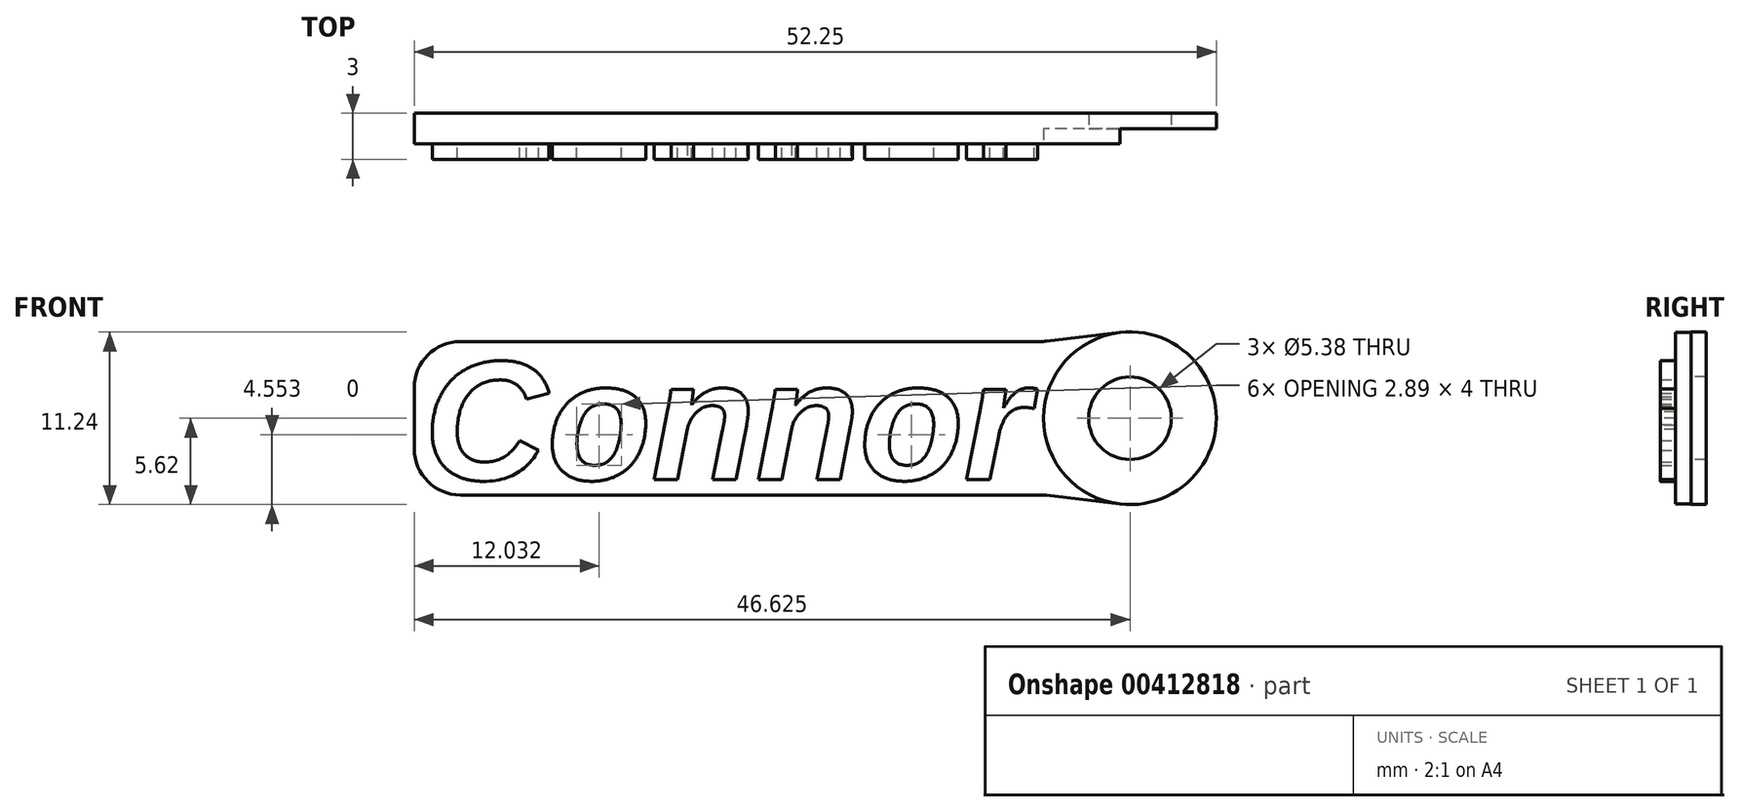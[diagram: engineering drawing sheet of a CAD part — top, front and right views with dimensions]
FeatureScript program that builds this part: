
annotation { "Feature Type Name" : "Feature", "Feature Type Description" : "" }
export const myFeature = defineFeature(function(context is Context, id is Id, definition is map)
    precondition{}
    {
        {
            var Q0;
            Q0=qCreatedBy(makeId("Front.planeOp"),FACE);
            var sketch = newSketch(context, id + "F0", { "sketchPlane" : qUnion([Q0])});
            skText(sketch, "E0", { "text": "Connor", "fontName": "Arimo-BoldItalic.ttf"});
            const initialGuessF0  = {"E0": [-0.02038, -0.008, 1, 0, 0.008]};
            skSetInitialGuess(sketch, initialGuessF0);
            skSolve(sketch);
        }
        {
            var Q0;
            Q0=qSketchRegion(id+"F0",true);
            extrude(context, id + "F1", {"entities" : qUnion([Q0]), "depth" : 1 * mm});
        }
        {
            var Q0;
            Q0=qCreatedBy(makeId("Front.planeOp"),FACE);
            var sketch = newSketch(context, id + "F2", { "sketchPlane" : qUnion([Q0])});
            skLineSegment(sketch, "E1", {"start": v(20, -9) * mm, "end": v(-21, -9) * mm});
            skLineSegment(sketch, "E2", {"start": v(-21, 1) * mm, "end": v(20, 1) * mm});
            skLineSegment(sketch, "E3", {"start": v(20, -9) * mm, "end": v(20, 1) * mm, "construction": true});
            skLineSegment(sketch, "E4", {"start": v(-21, -9) * mm, "end": v(-21, 1) * mm});
            skCircle(sketch, "E5", {"center": v(25.63, -4) * mm, "radius": 5.62 * mm});
            skLineSegment(sketch, "E6", {"start": v(20, -4) * mm, "end": v(67.35, -4) * mm, "construction": true});
            skPoint(sketch, "E6.endSnap0", {"position": v(20, -4) * mm});
            skLineSegment(sketch, "E7", {"start": v(20, 1) * mm, "end": v(24.97, 1.59) * mm});
            skLineSegment(sketch, "E8", {"start": v(24.97, -9.59) * mm, "end": v(20, -9) * mm});
            skCircle(sketch, "E9", {"center": v(25.63, -4) * mm, "radius": 2.69 * mm});
            skLineSegment(sketch, "E10", {"start": v(-20.38, 0) * mm, "end": v(-20.38, 1) * mm, "construction": true});
            skLineSegment(sketch, "E11", {"start": v(-20.38, -8) * mm, "end": v(-20.38, -9) * mm, "construction": true});
            skSolve(sketch);
        }
        {
            var Q0;
            Q0=qSketchRegion(id+"F2",true);
            extrude(context, id + "F3", {"entities" : qUnion([Q0]), "oppositeDirection" : true, "depth" : 2 * mm});
        }
        {
            var Q0;
            Q0=makeQuery(id+"F3.opExtrude","SWEPT_EDGE",EDGE,{"disambiguationData":[OSD([sQuery(id+"F2.wireOp",EDGE,"E2"),sQuery(id+"F2.wireOp",EDGE,"E4")])]});
            var Q1;
            Q1=makeQuery(id+"F3.opExtrude","SWEPT_EDGE",EDGE,{"disambiguationData":[OSD([sQuery(id+"F2.wireOp",EDGE,"E1"),sQuery(id+"F2.wireOp",EDGE,"E4")])]});
            var Q2;
            Q2=makeQuery(id+"F3.opExtrude","SWEPT_EDGE",EDGE,{"disambiguationData":[OSD([sQuery(id+"F2.wireOp",EDGE,"E1"),sQuery(id+"F2.wireOp",EDGE,"E8")])]});
            var Q3;
            Q3=makeQuery(id+"F3.opExtrude","SWEPT_EDGE",EDGE,{"disambiguationData":[OSD([sQuery(id+"F2.wireOp",EDGE,"E2"),sQuery(id+"F2.wireOp",EDGE,"E7")])]});
            fillet(context, id + "F4", {"entities" : qUnion([Q0, Q1, Q2, Q3]), "radius" : 3 * mm, "tangentPropagation" : true, "allowEdgeOverflow" : false});
        }
        {
            var Q0;
            Q0=makeQuery(id+"F3.opExtrude","CAP_FACE",FACE,{"disambiguationData":[OSD([sQuery(id+"F2.wireOp",EDGE,"E1"),sQuery(id+"F2.wireOp",EDGE,"E2"),sQuery(id+"F2.wireOp",EDGE,"E4"),sQuery(id+"F2.wireOp",EDGE,"E5"),sQuery(id+"F2.wireOp",EDGE,"E7"),sQuery(id+"F2.wireOp",EDGE,"E8"),sQuery(id+"F2.wireOp",EDGE,"E9")])],"isStart":true});
            var sketch = newSketch(context, id + "F5", { "sketchPlane" : qUnion([Q0])});
            skCircle(sketch, "E12", {"center": v(25.63, -4) * mm, "radius": 5.62 * mm});
            skSolve(sketch);
        }
        {
            var Q0;
            Q0=qSketchRegion(id+"F5",true);
            extrude(context, id + "F6", {"entities" : qUnion([Q0]), "operationType" : NewBodyOperationType.REMOVE, "oppositeDirection" : true, "depth" : 1 * mm});
        }
    });
